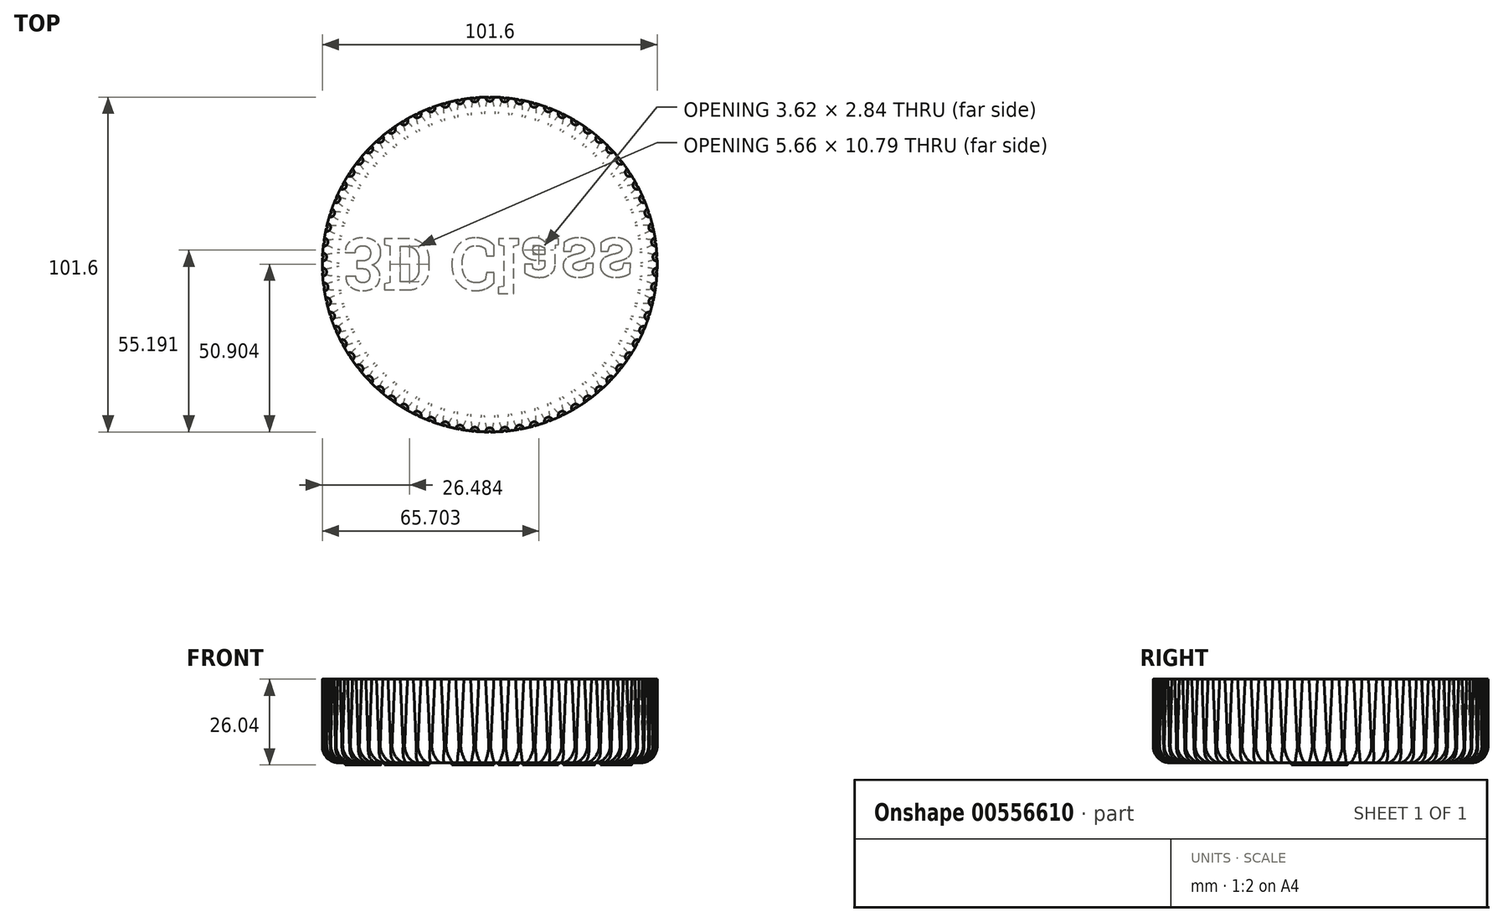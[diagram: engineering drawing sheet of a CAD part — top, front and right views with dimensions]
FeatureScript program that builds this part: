
annotation { "Feature Type Name" : "Feature", "Feature Type Description" : "" }
export const myFeature = defineFeature(function(context is Context, id is Id, definition is map)
    precondition{}
    {
        {
            var Q0;
            Q0=qCreatedBy(makeId("Top.planeOp"),FACE);
            var sketch = newSketch(context, id + "F0", { "sketchPlane" : qUnion([Q0])});
            skCircle(sketch, "E0", {"center": v(0, 0) * mm, "radius": 50.8 * mm});
            skSolve(sketch);
        }
        {
            var Q0;
            Q0 = qSketchRegion(id + "F0", true);
            extrude(context, id + "F1", {"entities" : qUnion([Q0]), "depth" : 25.4 * mm, "offsetDistance" : 25.4 * mm});
        }
        {
            var Q0;
            Q0=makeQuery(id+"F1.opExtrude","CAP_FACE",FACE,{"disambiguationData":[OSD([sQuery(id+"F0.wireOp",EDGE,"E0")])],"isStart":false});
            var sketch = newSketch(context, id + "F2", { "sketchPlane" : qUnion([Q0])});
            skCircle(sketch, "E1", {"center": v(0, 50.8) * mm, "radius": 1.27 * mm});
            skCircle(sketch, "E2.1.0", {"center": v(-4.55, 50.6) * mm, "radius": 1.27 * mm});
            skCircle(sketch, "E2.2.0", {"center": v(-9.07, 49.98) * mm, "radius": 1.27 * mm});
            skCircle(sketch, "E2.3.0", {"center": v(-13.51, 48.97) * mm, "radius": 1.27 * mm});
            skCircle(sketch, "E2.4.0", {"center": v(-17.85, 47.56) * mm, "radius": 1.27 * mm});
            skCircle(sketch, "E2.5.0", {"center": v(-22.04, 45.77) * mm, "radius": 1.27 * mm});
            skCircle(sketch, "E2.6.0", {"center": v(-26.06, 43.6) * mm, "radius": 1.27 * mm});
            skCircle(sketch, "E2.7.0", {"center": v(-29.86, 41.1) * mm, "radius": 1.27 * mm});
            skCircle(sketch, "E2.8.0", {"center": v(-33.42, 38.26) * mm, "radius": 1.27 * mm});
            skCircle(sketch, "E2.9.0", {"center": v(-36.72, 35.1) * mm, "radius": 1.27 * mm});
            skCircle(sketch, "E2.10.0", {"center": v(-39.72, 31.67) * mm, "radius": 1.27 * mm});
            skCircle(sketch, "E2.11.0", {"center": v(-42.4, 27.99) * mm, "radius": 1.27 * mm});
            skCircle(sketch, "E2.12.0", {"center": v(-44.73, 24.07) * mm, "radius": 1.27 * mm});
            skCircle(sketch, "E2.13.0", {"center": v(-46.71, 19.97) * mm, "radius": 1.27 * mm});
            skCircle(sketch, "E2.14.0", {"center": v(-48.31, 15.7) * mm, "radius": 1.27 * mm});
            skCircle(sketch, "E2.15.0", {"center": v(-49.53, 11.3) * mm, "radius": 1.27 * mm});
            skCircle(sketch, "E2.16.0", {"center": v(-50.34, 6.82) * mm, "radius": 1.27 * mm});
            skCircle(sketch, "E2.17.0", {"center": v(-50.75, 2.28) * mm, "radius": 1.27 * mm});
            skCircle(sketch, "E2.18.0", {"center": v(-50.75, -2.28) * mm, "radius": 1.27 * mm});
            skCircle(sketch, "E2.19.0", {"center": v(-50.34, -6.82) * mm, "radius": 1.27 * mm});
            skCircle(sketch, "E2.20.0", {"center": v(-49.53, -11.3) * mm, "radius": 1.27 * mm});
            skCircle(sketch, "E2.21.0", {"center": v(-48.31, -15.7) * mm, "radius": 1.27 * mm});
            skCircle(sketch, "E2.22.0", {"center": v(-46.71, -19.97) * mm, "radius": 1.27 * mm});
            skCircle(sketch, "E2.23.0", {"center": v(-44.73, -24.07) * mm, "radius": 1.27 * mm});
            skCircle(sketch, "E2.24.0", {"center": v(-42.4, -27.99) * mm, "radius": 1.27 * mm});
            skCircle(sketch, "E2.25.0", {"center": v(-39.72, -31.67) * mm, "radius": 1.27 * mm});
            skCircle(sketch, "E2.26.0", {"center": v(-36.72, -35.1) * mm, "radius": 1.27 * mm});
            skCircle(sketch, "E2.27.0", {"center": v(-33.42, -38.26) * mm, "radius": 1.27 * mm});
            skCircle(sketch, "E2.28.0", {"center": v(-29.86, -41.1) * mm, "radius": 1.27 * mm});
            skCircle(sketch, "E2.29.0", {"center": v(-26.06, -43.6) * mm, "radius": 1.27 * mm});
            skCircle(sketch, "E2.30.0", {"center": v(-22.04, -45.77) * mm, "radius": 1.27 * mm});
            skCircle(sketch, "E2.31.0", {"center": v(-17.85, -47.56) * mm, "radius": 1.27 * mm});
            skCircle(sketch, "E2.32.0", {"center": v(-13.51, -48.97) * mm, "radius": 1.27 * mm});
            skCircle(sketch, "E2.33.0", {"center": v(-9.07, -49.98) * mm, "radius": 1.27 * mm});
            skCircle(sketch, "E2.34.0", {"center": v(-4.55, -50.6) * mm, "radius": 1.27 * mm});
            skCircle(sketch, "E2.35.0", {"center": v(0, -50.8) * mm, "radius": 1.27 * mm});
            skCircle(sketch, "E2.36.0", {"center": v(4.55, -50.6) * mm, "radius": 1.27 * mm});
            skCircle(sketch, "E2.37.0", {"center": v(9.07, -49.98) * mm, "radius": 1.27 * mm});
            skCircle(sketch, "E2.38.0", {"center": v(13.51, -48.97) * mm, "radius": 1.27 * mm});
            skCircle(sketch, "E2.39.0", {"center": v(17.85, -47.56) * mm, "radius": 1.27 * mm});
            skCircle(sketch, "E2.40.0", {"center": v(22.04, -45.77) * mm, "radius": 1.27 * mm});
            skCircle(sketch, "E2.41.0", {"center": v(26.06, -43.6) * mm, "radius": 1.27 * mm});
            skCircle(sketch, "E2.42.0", {"center": v(29.86, -41.1) * mm, "radius": 1.27 * mm});
            skCircle(sketch, "E2.43.0", {"center": v(33.42, -38.26) * mm, "radius": 1.27 * mm});
            skCircle(sketch, "E2.44.0", {"center": v(36.72, -35.1) * mm, "radius": 1.27 * mm});
            skCircle(sketch, "E2.45.0", {"center": v(39.72, -31.67) * mm, "radius": 1.27 * mm});
            skCircle(sketch, "E2.46.0", {"center": v(42.4, -27.99) * mm, "radius": 1.27 * mm});
            skCircle(sketch, "E2.47.0", {"center": v(44.73, -24.07) * mm, "radius": 1.27 * mm});
            skCircle(sketch, "E2.48.0", {"center": v(46.71, -19.97) * mm, "radius": 1.27 * mm});
            skCircle(sketch, "E2.49.0", {"center": v(48.31, -15.7) * mm, "radius": 1.27 * mm});
            skCircle(sketch, "E2.50.0", {"center": v(49.53, -11.3) * mm, "radius": 1.27 * mm});
            skCircle(sketch, "E2.51.0", {"center": v(50.34, -6.82) * mm, "radius": 1.27 * mm});
            skCircle(sketch, "E2.52.0", {"center": v(50.75, -2.28) * mm, "radius": 1.27 * mm});
            skCircle(sketch, "E2.53.0", {"center": v(50.75, 2.28) * mm, "radius": 1.27 * mm});
            skCircle(sketch, "E2.54.0", {"center": v(50.34, 6.82) * mm, "radius": 1.27 * mm});
            skCircle(sketch, "E2.55.0", {"center": v(49.53, 11.3) * mm, "radius": 1.27 * mm});
            skCircle(sketch, "E2.56.0", {"center": v(48.31, 15.7) * mm, "radius": 1.27 * mm});
            skCircle(sketch, "E2.57.0", {"center": v(46.71, 19.97) * mm, "radius": 1.27 * mm});
            skCircle(sketch, "E2.58.0", {"center": v(44.73, 24.07) * mm, "radius": 1.27 * mm});
            skCircle(sketch, "E2.59.0", {"center": v(42.4, 27.99) * mm, "radius": 1.27 * mm});
            skCircle(sketch, "E2.60.0", {"center": v(39.72, 31.67) * mm, "radius": 1.27 * mm});
            skCircle(sketch, "E2.61.0", {"center": v(36.72, 35.1) * mm, "radius": 1.27 * mm});
            skCircle(sketch, "E2.62.0", {"center": v(33.42, 38.26) * mm, "radius": 1.27 * mm});
            skCircle(sketch, "E2.63.0", {"center": v(29.86, 41.1) * mm, "radius": 1.27 * mm});
            skCircle(sketch, "E2.64.0", {"center": v(26.06, 43.6) * mm, "radius": 1.27 * mm});
            skCircle(sketch, "E2.65.0", {"center": v(22.04, 45.77) * mm, "radius": 1.27 * mm});
            skCircle(sketch, "E2.66.0", {"center": v(17.85, 47.56) * mm, "radius": 1.27 * mm});
            skCircle(sketch, "E2.67.0", {"center": v(13.51, 48.97) * mm, "radius": 1.27 * mm});
            skCircle(sketch, "E2.68.0", {"center": v(9.07, 49.98) * mm, "radius": 1.27 * mm});
            skCircle(sketch, "E2.69.0", {"center": v(4.55, 50.6) * mm, "radius": 1.27 * mm});
            skPoint(sketch, "E2.center", {"position": v(0, 0) * mm});
            skSolve(sketch);
        }
        {
            var Q0;
            Q0 = qSketchRegion(id + "F2", true);
            extrude(context, id + "F3", {"entities" : qUnion([Q0]), "operationType" : NewBodyOperationType.REMOVE, "oppositeDirection" : true, "depth" : 25.4 * mm, "offsetDistance" : 25.4 * mm, "hasDraft" : true, "draftAngle" : 2.8 * degree, "draftPullDirection" : true});
        }
        {
            var Q0;
            Q0=makeQuery(id+"F1.opExtrude","CAP_FACE",FACE,{"disambiguationData":[OSD([sQuery(id+"F0.wireOp",EDGE,"E0")])],"isStart":true});
            fillet(context, id + "F4", {"entities" : qUnion([Q0]), "radius" : 5.08 * mm, "tangentPropagation" : true, "allowEdgeOverflow" : false});
        }
        {
            var Q0;
            Q0=makeQuery(id+"F1.opExtrude","CAP_FACE",FACE,{"disambiguationData":[OSD([sQuery(id+"F0.wireOp",EDGE,"E0")])],"isStart":true});
            var sketch = newSketch(context, id + "F5", { "sketchPlane" : qUnion([Q0])});
            skText(sketch, "E3", { "text": "3D Class", "fontName": "RobotoSlab-Bold.ttf"});
            const initialGuessF5  = {"E3": [-0.04445, -0.0079, 1, 0, 0.0158]};
            skSetInitialGuess(sketch, initialGuessF5);
            skSolve(sketch);
        }
        {
            var Q0;
            Q0 = qSketchRegion(id + "F5", true);
            extrude(context, id + "F6", {"entities" : qUnion([Q0]), "depth" : 0.64 * mm, "offsetDistance" : 25.4 * mm});
        }
    });
